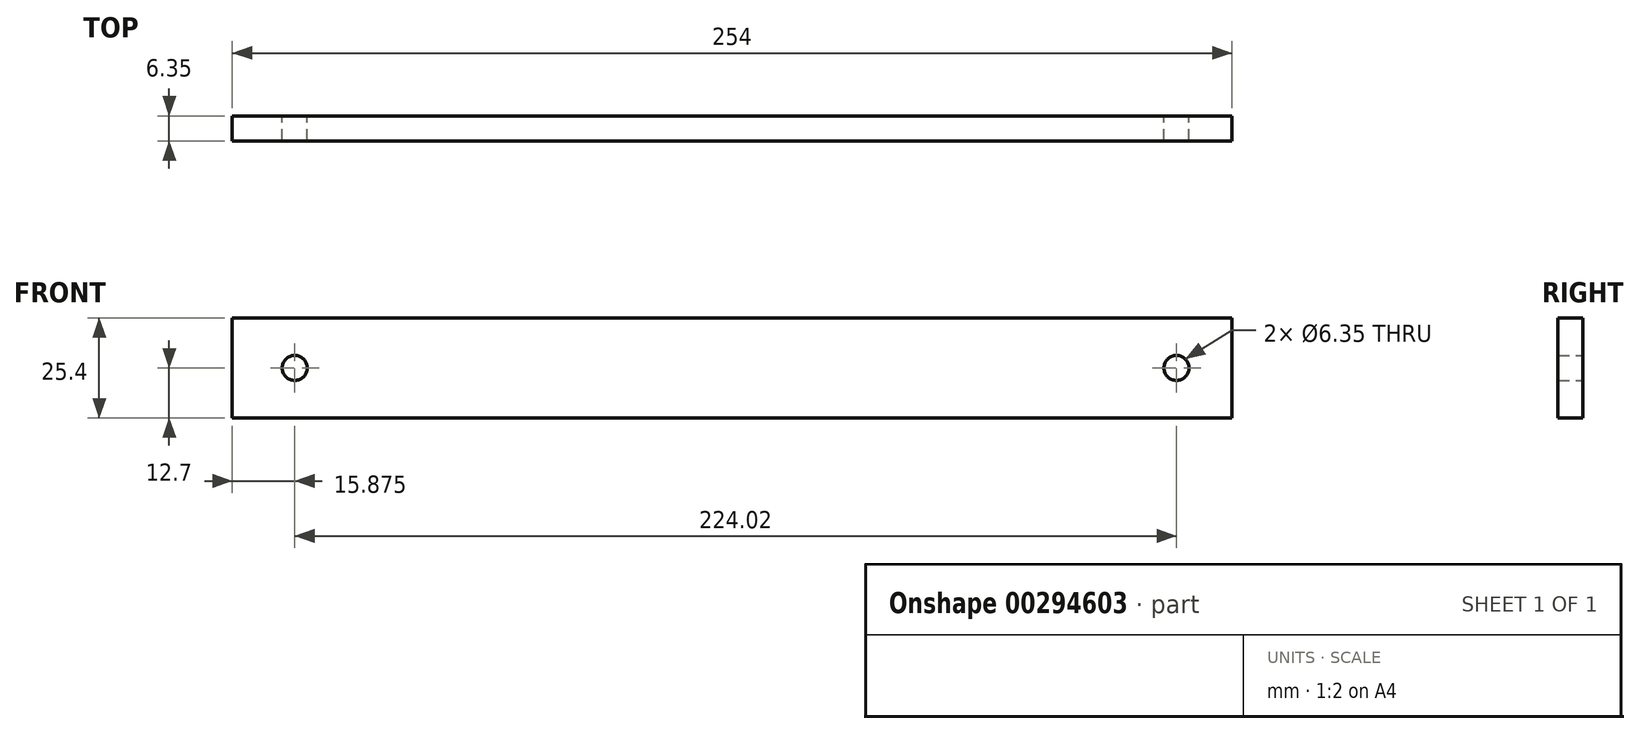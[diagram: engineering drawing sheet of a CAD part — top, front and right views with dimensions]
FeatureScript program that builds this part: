
annotation { "Feature Type Name" : "Feature", "Feature Type Description" : "" }
export const myFeature = defineFeature(function(context is Context, id is Id, definition is map)
    precondition{}
    {
        {
            var Q0;
            Q0=qCreatedBy(makeId("Front.planeOp"),FACE);
            var sketch = newSketch(context, id + "F0", { "sketchPlane" : qUnion([Q0])});
            skLineSegment(sketch, "E0.bottom", {"start": v(-127, -12.7) * mm, "end": v(127, -12.7) * mm});
            skLineSegment(sketch, "E0.top", {"start": v(-127, 12.7) * mm, "end": v(127, 12.7) * mm});
            skLineSegment(sketch, "E0.left", {"start": v(-127, -12.7) * mm, "end": v(-127, 12.7) * mm});
            skLineSegment(sketch, "E0.right", {"start": v(127, -12.7) * mm, "end": v(127, 12.7) * mm});
            skPoint(sketch, "E0.middle", {"position": v(0, 0) * mm});
            skCircle(sketch, "E1", {"center": v(-111.12, 0) * mm, "radius": 3.18 * mm});
            skCircle(sketch, "E2", {"center": v(112.9, 0) * mm, "radius": 3.18 * mm});
            skSolve(sketch);
        }
        {
            var Q0;
            Q0=makeQuery(id+"F0.imprint","IMPRINT",FACE,{"disambiguationData":[TD([[makeQuery(id+"F0.imprint","IMPRINT",EDGE,{"derivedFrom":sQuery(id+"F0.wireOp",EDGE,"E0.bottom")}),1.0]])]});
            extrude(context, id + "F1", {"entities" : qUnion([Q0]), "depth" : 6.35 * mm});
        }
    });
